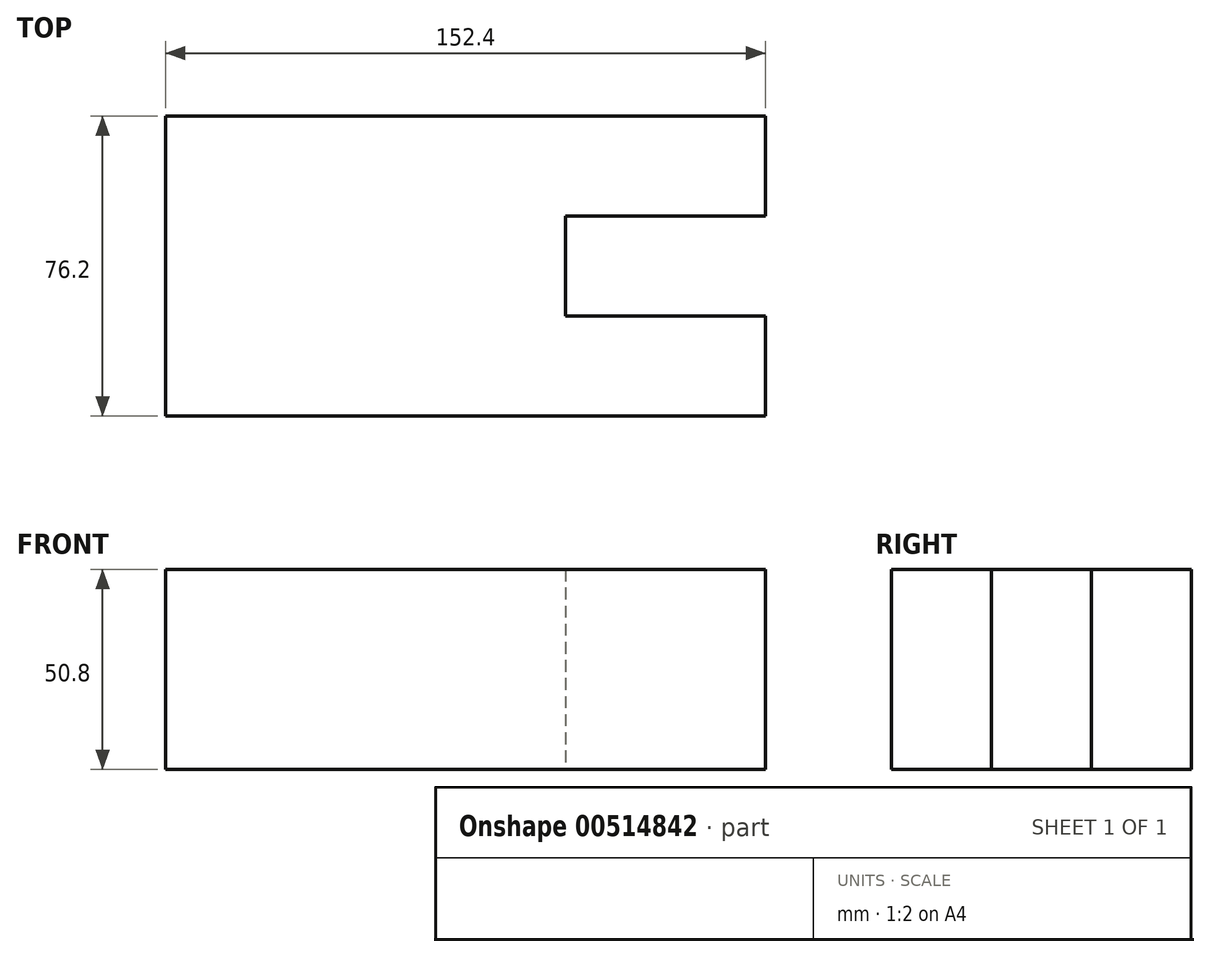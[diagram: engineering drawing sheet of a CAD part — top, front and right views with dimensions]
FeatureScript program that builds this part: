
annotation { "Feature Type Name" : "Feature", "Feature Type Description" : "" }
export const myFeature = defineFeature(function(context is Context, id is Id, definition is map)
    precondition{}
    {
        {
            var Q0;
            Q0=qCreatedBy(makeId("Top.planeOp"),FACE);
            var sketch = newSketch(context, id + "F0", { "sketchPlane" : qUnion([Q0])});
            skLineSegment(sketch, "E0", {"start": v(-74.82, 64.4) * mm, "end": v(77.58, 64.4) * mm});
            skLineSegment(sketch, "E1", {"start": v(77.58, 64.4) * mm, "end": v(77.58, 39) * mm});
            skLineSegment(sketch, "E2", {"start": v(77.58, 39) * mm, "end": v(26.78, 39) * mm});
            skLineSegment(sketch, "E3", {"start": v(26.78, 39) * mm, "end": v(26.78, 13.6) * mm});
            skLineSegment(sketch, "E4", {"start": v(26.78, 13.6) * mm, "end": v(77.58, 13.6) * mm});
            skLineSegment(sketch, "E5", {"start": v(77.58, 13.6) * mm, "end": v(77.58, -11.8) * mm});
            skLineSegment(sketch, "E6", {"start": v(77.58, -11.8) * mm, "end": v(-74.82, -11.8) * mm});
            skLineSegment(sketch, "E7", {"start": v(-74.82, 64.4) * mm, "end": v(-74.82, -11.8) * mm});
            skSolve(sketch);
        }
        {
            var Q0;
            Q0 = qSketchRegion(id + "F0", true);
            extrude(context, id + "F1", {"entities" : qUnion([Q0]), "depth" : 50.8 * mm, "offsetDistance" : 25.4 * mm});
        }
    });
